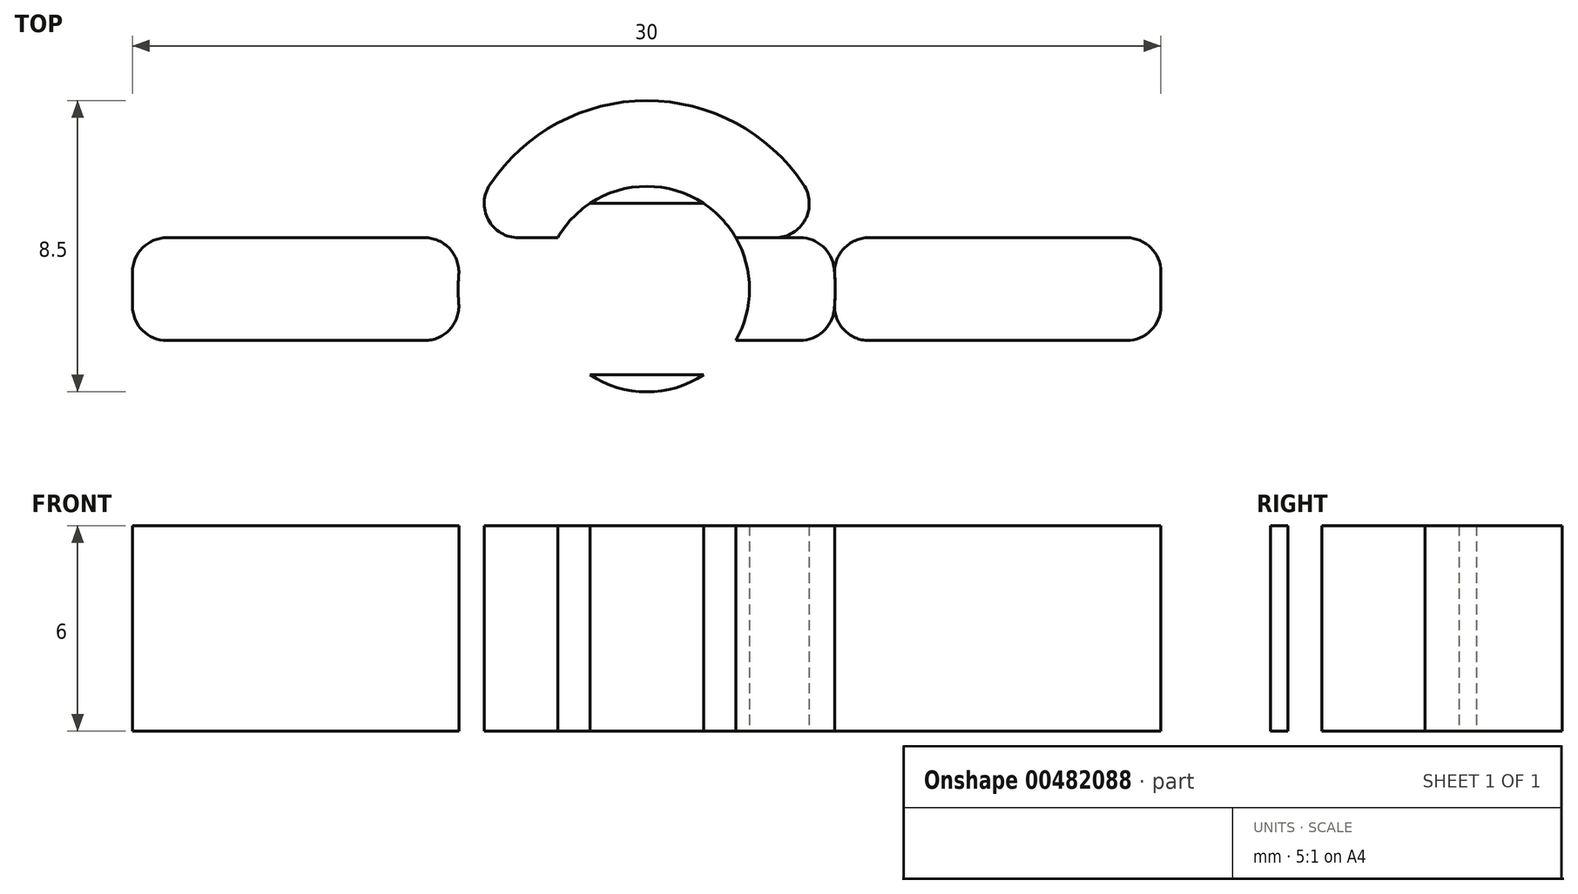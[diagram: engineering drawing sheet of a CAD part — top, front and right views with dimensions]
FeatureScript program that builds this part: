
annotation { "Feature Type Name" : "Feature", "Feature Type Description" : "" }
export const myFeature = defineFeature(function(context is Context, id is Id, definition is map)
    precondition{}
    {
        {
            var Q0;
            Q0=qCreatedBy(makeId("Top.planeOp"),FACE);
            var sketch = newSketch(context, id + "F0", { "sketchPlane" : qUnion([Q0])});
            skCircle(sketch, "E0", {"center": v(0, 0) * mm, "radius": 5.5 * mm});
            skCircle(sketch, "E1", {"center": v(0, 0) * mm, "radius": 3 * mm});
            skLineSegment(sketch, "E2.bottom", {"start": v(-15, 1.5) * mm, "end": v(15, 1.5) * mm});
            skLineSegment(sketch, "E2.top", {"start": v(-15, -1.5) * mm, "end": v(15, -1.5) * mm});
            skLineSegment(sketch, "E2.left", {"start": v(-15, 1.5) * mm, "end": v(-15, -1.5) * mm});
            skLineSegment(sketch, "E2.right", {"start": v(15, 1.5) * mm, "end": v(15, -1.5) * mm});
            skLineSegment(sketch, "E3", {"start": v(-1.66, 2.5) * mm, "end": v(1.66, 2.5) * mm});
            skLineSegment(sketch, "E4", {"start": v(1.66, -2.5) * mm, "end": v(-1.66, -2.5) * mm});
            skSolve(sketch);
        }
        {
            var Q0;
            {var subQ3=sQuery(id+"F0.wireOp",EDGE,"E2.top");var subQ6=sQuery(id+"F0.wireOp",EDGE,"E0");var subQ9=makeQuery(id+"F0.imprint","INTERSECT",VERTEX,{"disambiguationData":[OD(0.0)],"derivedFrom":[subQ6,subQ3]});Q0=makeQuery(id+"F0.imprint","IMPRINT",FACE,{"disambiguationData":[TD([[makeQuery(id+"F0.imprint","IMPRINT",EDGE,{"disambiguationData":[TD([[subQ9,-1.0]])],"derivedFrom":subQ6}),1.0]])]});}
            var Q1;
            {var subQ5=sQuery(id+"F0.wireOp",EDGE,"E2.left");Q1=makeQuery(id+"F0.imprint","IMPRINT",FACE,{"disambiguationData":[TD([[makeQuery(id+"F0.imprint","IMPRINT",EDGE,{"derivedFrom":subQ5}),1.0]])]});}
            var Q2;
            {var subQ0=sQuery(id+"F0.wireOp",EDGE,"E2.bottom");var subQ1=sQuery(id+"F0.wireOp",EDGE,"E0");var subQ2=makeQuery(id+"F0.imprint","INTERSECT",VERTEX,{"disambiguationData":[OD(0.0)],"derivedFrom":[subQ1,subQ0]});Q2=makeQuery(id+"F0.imprint","IMPRINT",FACE,{"disambiguationData":[TD([[makeQuery(id+"F0.imprint","IMPRINT",EDGE,{"disambiguationData":[TD([[subQ2,-1.0]])],"derivedFrom":subQ1}),1.0]])]});}
            var Q3;
            {var subQ5=sQuery(id+"F0.wireOp",EDGE,"E2.right");Q3=makeQuery(id+"F0.imprint","IMPRINT",FACE,{"disambiguationData":[TD([[makeQuery(id+"F0.imprint","IMPRINT",EDGE,{"derivedFrom":subQ5}),-1.0]])]});}
            var Q4;
            {var subQ0=sQuery(id+"F0.wireOp",EDGE,"E2.bottom");var subQ1=sQuery(id+"F0.wireOp",EDGE,"E0");var subQ2=makeQuery(id+"F0.imprint","INTERSECT",VERTEX,{"disambiguationData":[OD(1.0)],"derivedFrom":[subQ1,subQ0]});Q4=makeQuery(id+"F0.imprint","IMPRINT",FACE,{"disambiguationData":[TD([[makeQuery(id+"F0.imprint","IMPRINT",EDGE,{"disambiguationData":[TD([[subQ2,1.0]])],"derivedFrom":subQ1}),1.0]])]});}
            var Q5;
            {var subQ3=sQuery(id+"F0.wireOp",EDGE,"E2.bottom");var subQ7=sQuery(id+"F0.wireOp",EDGE,"E0");var subQ9=makeQuery(id+"F0.imprint","INTERSECT",VERTEX,{"disambiguationData":[OD(0.0)],"derivedFrom":[subQ7,subQ3]});Q5=makeQuery(id+"F0.imprint","IMPRINT",FACE,{"disambiguationData":[TD([[makeQuery(id+"F0.imprint","IMPRINT",EDGE,{"disambiguationData":[TD([[subQ9,1.0]])],"derivedFrom":subQ7}),1.0]])]});}
            var Q6;
            {var subQ0=sQuery(id+"F0.wireOp",EDGE,"E3");Q6=makeQuery(id+"F0.imprint","IMPRINT",FACE,{"disambiguationData":[TD([[makeQuery(id+"F0.imprint","IMPRINT",EDGE,{"derivedFrom":subQ0}),1.0]])]});}
            var Q7;
            {var subQ0=sQuery(id+"F0.wireOp",EDGE,"E4");Q7=makeQuery(id+"F0.imprint","IMPRINT",FACE,{"disambiguationData":[TD([[makeQuery(id+"F0.imprint","IMPRINT",EDGE,{"derivedFrom":subQ0}),1.0]])]});}
            extrude(context, id + "F1", {"entities" : qUnion([Q0, Q1, Q2, Q3, Q4, Q5, Q6, Q7]), "depth" : 6 * mm, "offsetDistance" : 25 * mm});
        }
        {
            var Q0;
            Q0=makeQuery(id+"F1.opExtrude","SWEPT_EDGE",EDGE,{"disambiguationData":[OSD([sQuery(id+"F0.wireOp",EDGE,"E2.top"),sQuery(id+"F0.wireOp",EDGE,"E2.right")])]});
            var Q1;
            Q1=makeQuery(id+"F1.opExtrude","SWEPT_EDGE",EDGE,{"disambiguationData":[OSD([sQuery(id+"F0.wireOp",EDGE,"E2.top"),sQuery(id+"F0.wireOp",EDGE,"E2.left")])]});
            var Q2;
            Q2=makeQuery(id+"F1.opExtrude","SWEPT_EDGE",EDGE,{"disambiguationData":[OSD([sQuery(id+"F0.wireOp",EDGE,"E2.bottom"),sQuery(id+"F0.wireOp",EDGE,"E2.right")])]});
            var Q3;
            Q3=makeQuery(id+"F1.opExtrude","SWEPT_EDGE",EDGE,{"disambiguationData":[OSD([sQuery(id+"F0.wireOp",EDGE,"E2.bottom"),sQuery(id+"F0.wireOp",EDGE,"E2.left")])]});
            fillet(context, id + "F2", {"entities" : qUnion([Q0, Q1, Q2, Q3]), "radius" : 1 * mm, "tangentPropagation" : true, "allowEdgeOverflow" : false});
        }
        {
            var Q0;
            {var subQ0=sQuery(id+"F0.wireOp",EDGE,"E2.top");var subQ1=sQuery(id+"F0.wireOp",EDGE,"E0");Q0=makeQuery(id+"F1.opExtrude","SWEPT_EDGE",EDGE,{"disambiguationData":[OSD([subQ1,subQ0]),TDD([makeQuery(id+"F0.imprint","INTERSECT",VERTEX,{"disambiguationData":[OD(1.0)],"derivedFrom":[subQ1,subQ0]})])]});}
            var Q1;
            {var subQ0=sQuery(id+"F0.wireOp",EDGE,"E2.top");var subQ1=sQuery(id+"F0.wireOp",EDGE,"E0");Q1=makeQuery(id+"F1.opExtrude","SWEPT_EDGE",EDGE,{"disambiguationData":[OSD([subQ1,subQ0]),TDD([makeQuery(id+"F0.imprint","INTERSECT",VERTEX,{"disambiguationData":[OD(0.0)],"derivedFrom":[subQ1,subQ0]})])]});}
            var Q2;
            {var subQ0=sQuery(id+"F0.wireOp",EDGE,"E2.bottom");var subQ1=sQuery(id+"F0.wireOp",EDGE,"E0");Q2=makeQuery(id+"F1.opExtrude","SWEPT_EDGE",EDGE,{"disambiguationData":[OSD([subQ1,subQ0]),TDD([makeQuery(id+"F0.imprint","INTERSECT",VERTEX,{"disambiguationData":[OD(0.0)],"derivedFrom":[subQ1,subQ0]})])]});}
            var Q3;
            {var subQ0=sQuery(id+"F0.wireOp",EDGE,"E2.bottom");var subQ1=sQuery(id+"F0.wireOp",EDGE,"E0");Q3=makeQuery(id+"F1.opExtrude","SWEPT_EDGE",EDGE,{"disambiguationData":[OSD([subQ1,subQ0]),TDD([makeQuery(id+"F0.imprint","INTERSECT",VERTEX,{"disambiguationData":[OD(1.0)],"derivedFrom":[subQ1,subQ0]})])]});}
            var Q4;
            {var subQ0=sQuery(id+"F0.wireOp",EDGE,"E3");var subQ1=sQuery(id+"F0.wireOp",EDGE,"E1");Q4=makeQuery(id+"F1.opExtrude","SWEPT_EDGE",EDGE,{"disambiguationData":[OSD([subQ1,subQ0]),TDD([makeQuery(id+"F0.imprint","INTERSECT",VERTEX,{"disambiguationData":[OD(0.0)],"derivedFrom":[subQ1,subQ0]})])]});}
            var Q5;
            {var subQ0=sQuery(id+"F0.wireOp",EDGE,"E3");var subQ1=sQuery(id+"F0.wireOp",EDGE,"E1");Q5=makeQuery(id+"F1.opExtrude","SWEPT_EDGE",EDGE,{"disambiguationData":[OSD([subQ1,subQ0]),TDD([makeQuery(id+"F0.imprint","INTERSECT",VERTEX,{"disambiguationData":[OD(1.0)],"derivedFrom":[subQ1,subQ0]})])]});}
            var Q6;
            {var subQ0=sQuery(id+"F0.wireOp",EDGE,"E4");var subQ1=sQuery(id+"F0.wireOp",EDGE,"E1");Q6=makeQuery(id+"F1.opExtrude","SWEPT_EDGE",EDGE,{"disambiguationData":[OSD([subQ1,subQ0]),TDD([makeQuery(id+"F0.imprint","INTERSECT",VERTEX,{"disambiguationData":[OD(0.0)],"derivedFrom":[subQ1,subQ0]})])]});}
            var Q7;
            {var subQ0=sQuery(id+"F0.wireOp",EDGE,"E4");var subQ1=sQuery(id+"F0.wireOp",EDGE,"E1");Q7=makeQuery(id+"F1.opExtrude","SWEPT_EDGE",EDGE,{"disambiguationData":[OSD([subQ1,subQ0]),TDD([makeQuery(id+"F0.imprint","INTERSECT",VERTEX,{"disambiguationData":[OD(1.0)],"derivedFrom":[subQ1,subQ0]})])]});}
            fillet(context, id + "F3", {"entities" : qUnion([Q0, Q1, Q2, Q3, Q4, Q5, Q6, Q7]), "radius" : 1 * mm, "tangentPropagation" : true, "allowEdgeOverflow" : false});
        }
    });
